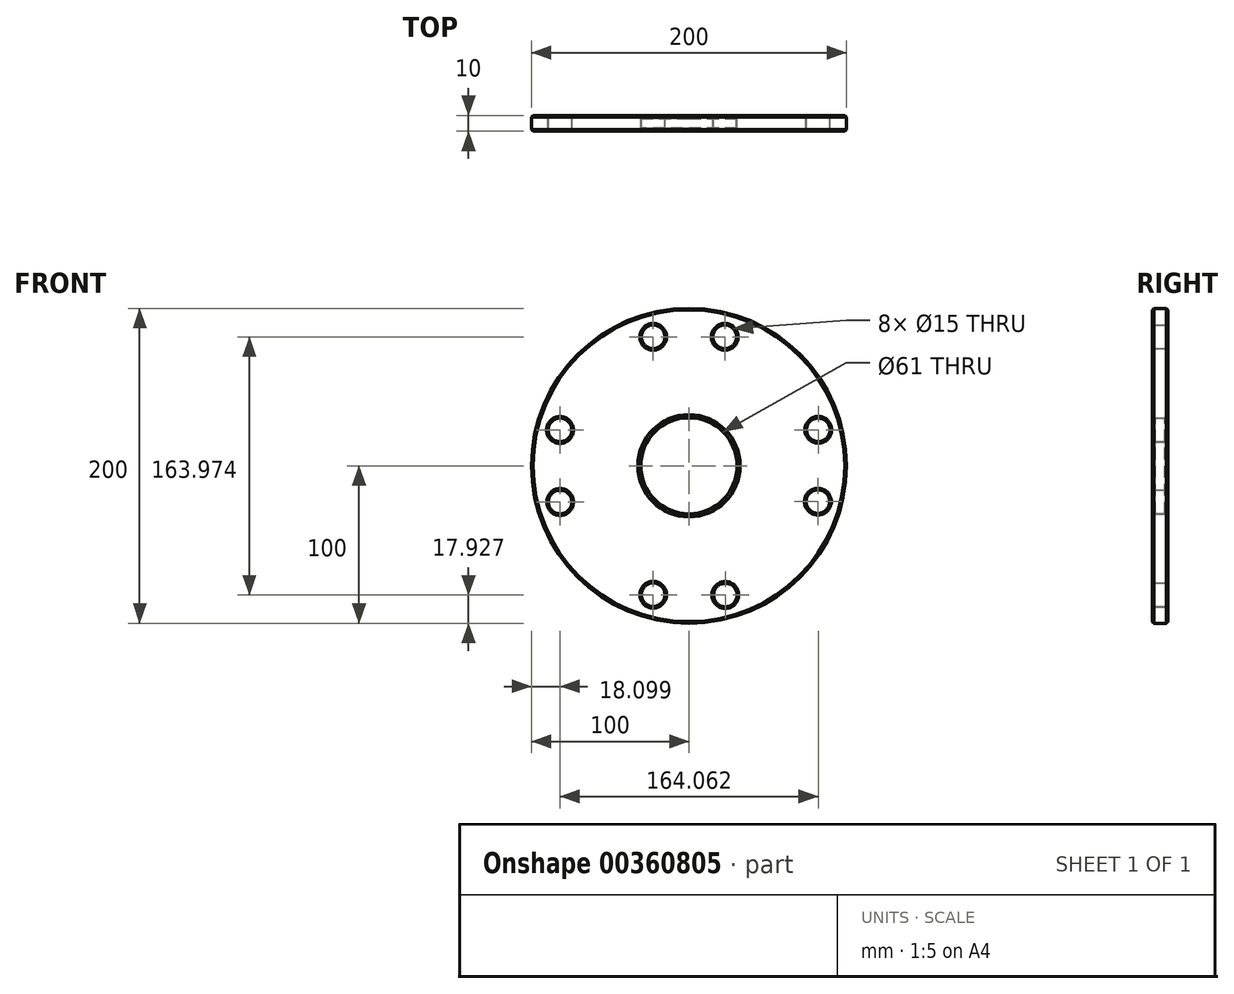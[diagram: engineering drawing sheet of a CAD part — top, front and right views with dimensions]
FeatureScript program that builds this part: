
annotation { "Feature Type Name" : "Feature", "Feature Type Description" : "" }
export const myFeature = defineFeature(function(context is Context, id is Id, definition is map)
    precondition{}
    {
        {
            var Q0;
            Q0=qCreatedBy(makeId("Front.planeOp"),FACE);
            var sketch = newSketch(context, id + "F0", { "sketchPlane" : qUnion([Q0])});
            skCircle(sketch, "E0", {"center": v(0, 0) * mm, "radius": 100 * mm});
            skCircle(sketch, "E1", {"center": v(0, 0) * mm, "radius": 30.5 * mm});
            skLineSegment(sketch, "E2", {"start": v(0, 0) * mm, "end": v(0, 100) * mm});
            skLineSegment(sketch, "E3", {"start": v(0, 0) * mm, "end": v(22.74, 81.9) * mm});
            skLineSegment(sketch, "E4", {"start": v(0, 0) * mm, "end": v(-22.74, 81.9) * mm});
            skCircle(sketch, "E5", {"center": v(-22.74, 81.9) * mm, "radius": 7.5 * mm});
            skCircle(sketch, "E6.1.0", {"center": v(-81.81, -23) * mm, "radius": 7.5 * mm});
            skCircle(sketch, "E6.2.0", {"center": v(23.1, -82.07) * mm, "radius": 7.5 * mm});
            skPoint(sketch, "E6.center", {"position": v(0.18, -0.09) * mm});
            skCircle(sketch, "E7.1.3.0", {"center": v(82.16, 22.83) * mm, "radius": 7.5 * mm});
            skCircle(sketch, "E8", {"center": v(22.74, 81.9) * mm, "radius": 7.5 * mm});
            skCircle(sketch, "E9.1.0", {"center": v(-81.9, 22.74) * mm, "radius": 7.5 * mm});
            skCircle(sketch, "E9.2.0", {"center": v(-22.74, -81.9) * mm, "radius": 7.5 * mm});
            skCircle(sketch, "E9.3.0", {"center": v(81.9, -22.74) * mm, "radius": 7.5 * mm});
            skSolve(sketch);
        }
        {
            var Q0;
            Q0=makeQuery(id+"F0.imprint","IMPRINT",FACE,{"disambiguationData":[TD([[makeQuery(id+"F0.imprint","IMPRINT",EDGE,{"derivedFrom":sQuery(id+"F0.wireOp",EDGE,"E0")}),1.0]])]});
            extrude(context, id + "F1", {"entities" : qUnion([Q0]), "depth" : 10 * mm});
        }
        {
            var Q0;
            Q0=makeQuery(id+"F1.opExtrude","CAP_EDGE",EDGE,{"disambiguationData":[OSD([sQuery(id+"F0.wireOp",EDGE,"E0")])],"isStart":true});
            chamfer(context, id + "F2", {"entities" : qUnion([Q0]), "chamferType" : ChamferType.OFFSET_ANGLE, "width" : 1 * mm, "oppositeDirection" : false, "angle" : 45 * degree, "tangentPropagation" : true});
        }
        {
            var Q0;
            Q0=makeQuery(id+"F1.opExtrude","CAP_EDGE",EDGE,{"disambiguationData":[OSD([sQuery(id+"F0.wireOp",EDGE,"E0")])],"isStart":false});
            chamfer(context, id + "F3", {"entities" : qUnion([Q0]), "chamferType" : ChamferType.OFFSET_ANGLE, "width" : 1 * mm, "oppositeDirection" : true, "angle" : 45 * degree, "tangentPropagation" : true});
        }
        {
            var Q0;
            Q0=makeQuery(id+"F1.opExtrude","CAP_EDGE",EDGE,{"disambiguationData":[OSD([sQuery(id+"F0.wireOp",EDGE,"E1")])],"isStart":true});
            chamfer(context, id + "F4", {"entities" : qUnion([Q0]), "chamferType" : ChamferType.OFFSET_ANGLE, "width" : 2 * mm, "oppositeDirection" : false, "angle" : 45 * degree, "tangentPropagation" : true});
        }
        {
            var Q0;
            Q0=makeQuery(id+"F1.opExtrude","CAP_EDGE",EDGE,{"disambiguationData":[OSD([sQuery(id+"F0.wireOp",EDGE,"E1")])],"isStart":false});
            chamfer(context, id + "F5", {"entities" : qUnion([Q0]), "chamferType" : ChamferType.OFFSET_ANGLE, "width" : 2 * mm, "oppositeDirection" : false, "angle" : 45 * degree, "tangentPropagation" : true});
        }
        {
            var Q0;
            Q0=makeQuery(id+"F1.opExtrude","CAP_EDGE",EDGE,{"disambiguationData":[OSD([sQuery(id+"F0.wireOp",EDGE,"E8")])],"isStart":true});
            var Q1;
            Q1=makeQuery(id+"F1.opExtrude","CAP_EDGE",EDGE,{"disambiguationData":[OSD([sQuery(id+"F0.wireOp",EDGE,"E5")])],"isStart":true});
            var Q2;
            Q2=makeQuery(id+"F1.opExtrude","CAP_EDGE",EDGE,{"disambiguationData":[OSD([sQuery(id+"F0.wireOp",EDGE,"E9.1.0")])],"isStart":true});
            var Q3;
            Q3=makeQuery(id+"F1.opExtrude","CAP_EDGE",EDGE,{"disambiguationData":[OSD([sQuery(id+"F0.wireOp",EDGE,"E6.1.0")])],"isStart":true});
            var Q4;
            Q4=makeQuery(id+"F1.opExtrude","CAP_EDGE",EDGE,{"disambiguationData":[OSD([sQuery(id+"F0.wireOp",EDGE,"E9.2.0")])],"isStart":true});
            var Q5;
            Q5=makeQuery(id+"F1.opExtrude","CAP_EDGE",EDGE,{"disambiguationData":[OSD([sQuery(id+"F0.wireOp",EDGE,"E6.2.0")])],"isStart":true});
            var Q6;
            Q6=makeQuery(id+"F1.opExtrude","CAP_EDGE",EDGE,{"disambiguationData":[OSD([sQuery(id+"F0.wireOp",EDGE,"E9.3.0")])],"isStart":true});
            var Q7;
            Q7=makeQuery(id+"F1.opExtrude","CAP_EDGE",EDGE,{"disambiguationData":[OSD([sQuery(id+"F0.wireOp",EDGE,"E7.1.3.0")])],"isStart":true});
            chamfer(context, id + "F6", {"entities" : qUnion([Q0, Q1, Q2, Q3, Q4, Q5, Q6, Q7]), "chamferType" : ChamferType.OFFSET_ANGLE, "width" : 1 * mm, "oppositeDirection" : false, "angle" : 45 * degree, "tangentPropagation" : true});
        }
        {
            var Q0;
            Q0=makeQuery(id+"F1.opExtrude","CAP_EDGE",EDGE,{"disambiguationData":[OSD([sQuery(id+"F0.wireOp",EDGE,"E5")])],"isStart":false});
            var Q1;
            Q1=makeQuery(id+"F1.opExtrude","CAP_EDGE",EDGE,{"disambiguationData":[OSD([sQuery(id+"F0.wireOp",EDGE,"E8")])],"isStart":false});
            var Q2;
            Q2=makeQuery(id+"F1.opExtrude","CAP_EDGE",EDGE,{"disambiguationData":[OSD([sQuery(id+"F0.wireOp",EDGE,"E7.1.3.0")])],"isStart":false});
            var Q3;
            Q3=makeQuery(id+"F1.opExtrude","CAP_EDGE",EDGE,{"disambiguationData":[OSD([sQuery(id+"F0.wireOp",EDGE,"E9.3.0")])],"isStart":false});
            var Q4;
            Q4=makeQuery(id+"F1.opExtrude","CAP_EDGE",EDGE,{"disambiguationData":[OSD([sQuery(id+"F0.wireOp",EDGE,"E6.2.0")])],"isStart":false});
            var Q5;
            Q5=makeQuery(id+"F1.opExtrude","CAP_EDGE",EDGE,{"disambiguationData":[OSD([sQuery(id+"F0.wireOp",EDGE,"E9.2.0")])],"isStart":false});
            var Q6;
            Q6=makeQuery(id+"F1.opExtrude","CAP_EDGE",EDGE,{"disambiguationData":[OSD([sQuery(id+"F0.wireOp",EDGE,"E9.1.0")])],"isStart":false});
            var Q7;
            Q7=makeQuery(id+"F1.opExtrude","CAP_EDGE",EDGE,{"disambiguationData":[OSD([sQuery(id+"F0.wireOp",EDGE,"E6.1.0")])],"isStart":false});
            chamfer(context, id + "F7", {"entities" : qUnion([Q0, Q1, Q2, Q3, Q4, Q5, Q6, Q7]), "chamferType" : ChamferType.OFFSET_ANGLE, "width" : 1 * mm, "oppositeDirection" : false, "angle" : 45 * degree, "tangentPropagation" : true});
        }
    });
